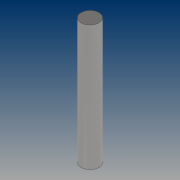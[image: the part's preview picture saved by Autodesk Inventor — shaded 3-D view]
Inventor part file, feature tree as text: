
AUTODESK INVENTOR PART (.ipt)
format: ipt  version: 2021 (Build 250183000, 183)  size: 75,264 bytes
history: native  units: mm
features: extrude x1, sketch x1
ambient origin geometry x8: Origin, YZ Plane, XZ Plane, XY Plane, X Axis, Y Axis, Z Axis, Center Point
bodies: Solid1 (feature_tree)
feature tree (2):
  extrude  "Extrusion1"  Depth=70.0mm TaperAngle=0.0deg
  sketch  "Sketch1"  dims[d0=10.0mm d1=70.0mm d2=0.0mm]
